# Revit family: Grohe_FlushPlate_SkateCosmopolitan_37535KF0
name_source: partatom
category: Plumbing Fixtures
units: mm (PartAtom-declared; Revit-internal decimal feet)

## family parameters
Cut with Voids When Loaded = No
Host = Face
OmniClass Number = 23.45.05.00
OmniClass Title = Sanitary Equipment
Part Type = Normal
Room Calculation Point = No
Round Connector Dimension = Use Diameter
Shared = No

## types (1)
- SKATE COSMOPOLITAN Flush Plate (37535KF0)
    Assembly Code = D2010
    AssetType = Fixed
    BIMObjectName = Grohe_FlushPlate_SkateCosmopolitan_37535KF0
    CO2NeutralProduction = GROHE is one of the first leading manufacturer within the sanitary industry having a CO2-neutral production.
    ClassificationName = Uniclass2015
    ClassificationValue = Pr_75_50_46_31
    Color = Black
    Cost = 0 $
    Default Elevation = 0 mm  [stored 0 ft]
    Description = for dual flush or start & stop actuation

for pneumatic discharge valve AV1, GD 2 cistern

vertical installation

130 x 172 mm

made of ABS

GROHE Long-Life finish

GROHE Water Saving - Less water, perfect flow

flush plate with magnetic holder and fixing brackets included

compatible with Rapid SLX

for use with Rapid SL and Uniset with GD 2 cistern please order shaft 40 911 000 (sold separately)

for use with Rapid SL and Uniset 0.82 m installation height please order shaft 40 950 000 (sold separately)
    DimensionsDocumentLink = https://cdn.cloud.grohe.com
    DocumentationCertificates = https://www.bimstore.co
    DocumentationInstallationGuide = https://www.bimstore.co
    DocumentationLiterature = https://www.bimstore.co
    DocumentationMaintenance = https://www.bimstore.co
    DocumentationTechnical = https://www.bimstore.co
    DurationUnit = Years
    EF000007 = Black
    EF000008 = 130
    EF000040 = 5
    EF001438 = 172
    EF002147 = Two button
    EF002169 = Plastic
    EF006331 = false
    EF006949 = Mechanical
    EF010109 = false
    EF020827 = true
    EF020828 = true
    EF023751 = true
    EF023752 = false
    Ecojoy = No
    ExpectedLife = 0
    FullRecyclabilityOfPlastic = All plastic components are fully recycable
    GROHESocialCommittment = green.grohe.com/social_engagement
    GROHESustainability = green.grohe.com
    IfcExportAs = IfcValve
    IfcExportType = IfcValveTypeEnum.FLUSHING
    Keynote = N13
    Manufacturer = Grohe
    ManufacturerName = Grohe
    Model = 37535KF0
    ModelNumber = 37535KF0
    ModelReference = Flush plate
    NBSDescription = Flush Control Devices
    NBSObjectName = Grohe - Flush Control Devices
    NBSReference = 90-15-35/470
    NominalDepth = 0 mm  [stored 0 ft]
    NominalHeight = 0 mm  [stored 0 ft]
    NominalLength = 0 mm  [stored 0 ft]
    PrimaryMaterial = Grohe_PhantomBlack
    ProductDescription = for dual flush or start & stop actuation

for pneumatic discharge valve AV1, GD 2 cistern

vertical installation

130 x 172 mm

made of ABS

GROHE Long-Life finish

GROHE Water Saving - Less water, perfect flow

flush plate with magnetic holder and fixing brackets included

compatible with Rapid SLX

for use with Rapid SL and Uniset with GD 2 cistern please order shaft 40 911 000 (sold separately)

for use with Rapid SL and Uniset 0.82 m installation height please order shaft 40 950 000 (sold separately)
    ProductNumber = 37535KF0
    ProductShortText = Flush plate
    ProductType = 101404
    ProductionYear = 2024
    SustainabilityAward = green.grohe.com/awards
    SustainabilityReport = green.grohe.com/reporting
    TPIDocumentLink = https://cdn.cloud.grohe.com
    Type Comments = SKATE COSMOPOLITAN Flush Plate (37535KF0)
    TypeName = SKATE COSMOPOLITAN Flush Plate (37535KF0)
    URL = https://www.grohe.co.uk
    WarrantyDurationLabor = 0
    WarrantyDurationParts = 0
    WarrantyDurationUnit = Years
    WarrantyGuarantorLabor = https://www.grohe.co.uk
    WarrantyGuarantorParts = https://www.grohe.co.uk
    _BSBibleVersion = 17
    _BimSpecGuid = 0
    _CurrentRevision = 1
    _DistributedBy = https://www.bimstore.co
    _ObjectUserGuide = https://www.bimstore.co

note: [stored X ft] marks values corroborated as IEEE doubles in the binary element streams (Revit-internal decimal feet)

## geometry (parser evidence)
native form markers: Sweep x2
no freeform markers — native parametric forms only
